# Revit family: QF_GIORIK_GM2011P_GR2011P
name_source: partatom
category: Specialty Equipment
revit_build: Autodesk Revit 2014 (Build: 20140709_2115(x64)
units: mm (PartAtom-declared; Revit-internal decimal feet)

## types (2) — shared parameters
Assembly Code = E1090320
Cold Water Connection Height = 145 mm  [stored 0.475722 ft]
Cold Water Size = 1"
Cold Water Temperature Recommended = 0 °C
Cycle = 50 Hz
FL Amps = 0 A
HP = 0
Indirect Waste Connection Height = 46 mm  [stored 0.150919 ft]
Indirect Waste Flow = 0.0 L/s
Indirect Waste Size = 1"
Manufacturer = GIORIK
Min Ckt Ampacity = 0 A
Phase = 3
URL = www.giorik.com
Volts = 400 V
Waste Water Discharge Temperature = 0 °C
Weight in Pounds = 485.017

## per-type parameters (varying)
| type | Apparent Power | Description | Max Overcurrent Protection | Watts |
| GR2011P | 16200 VA | HOLDING CABINET-REGENERATOR 20 GN 1/1 - PROGRAMMABLE ELECTRONIC VERSION | 20 A | 16200 W |
| GM2011P | 7200 VA | HOLDING CABINET 20 GN 1/1 - PROGRAMMABLE ELECTRONIC VERSION | 16 A | 7200 W |

note: column(s) folded — value = type name in every type: Model

note: [stored X ft] marks values corroborated as IEEE doubles in the binary element streams (Revit-internal decimal feet)

## geometry (parser evidence)
native form markers: Blend x13, Sweep x1
no freeform markers — native parametric forms only
